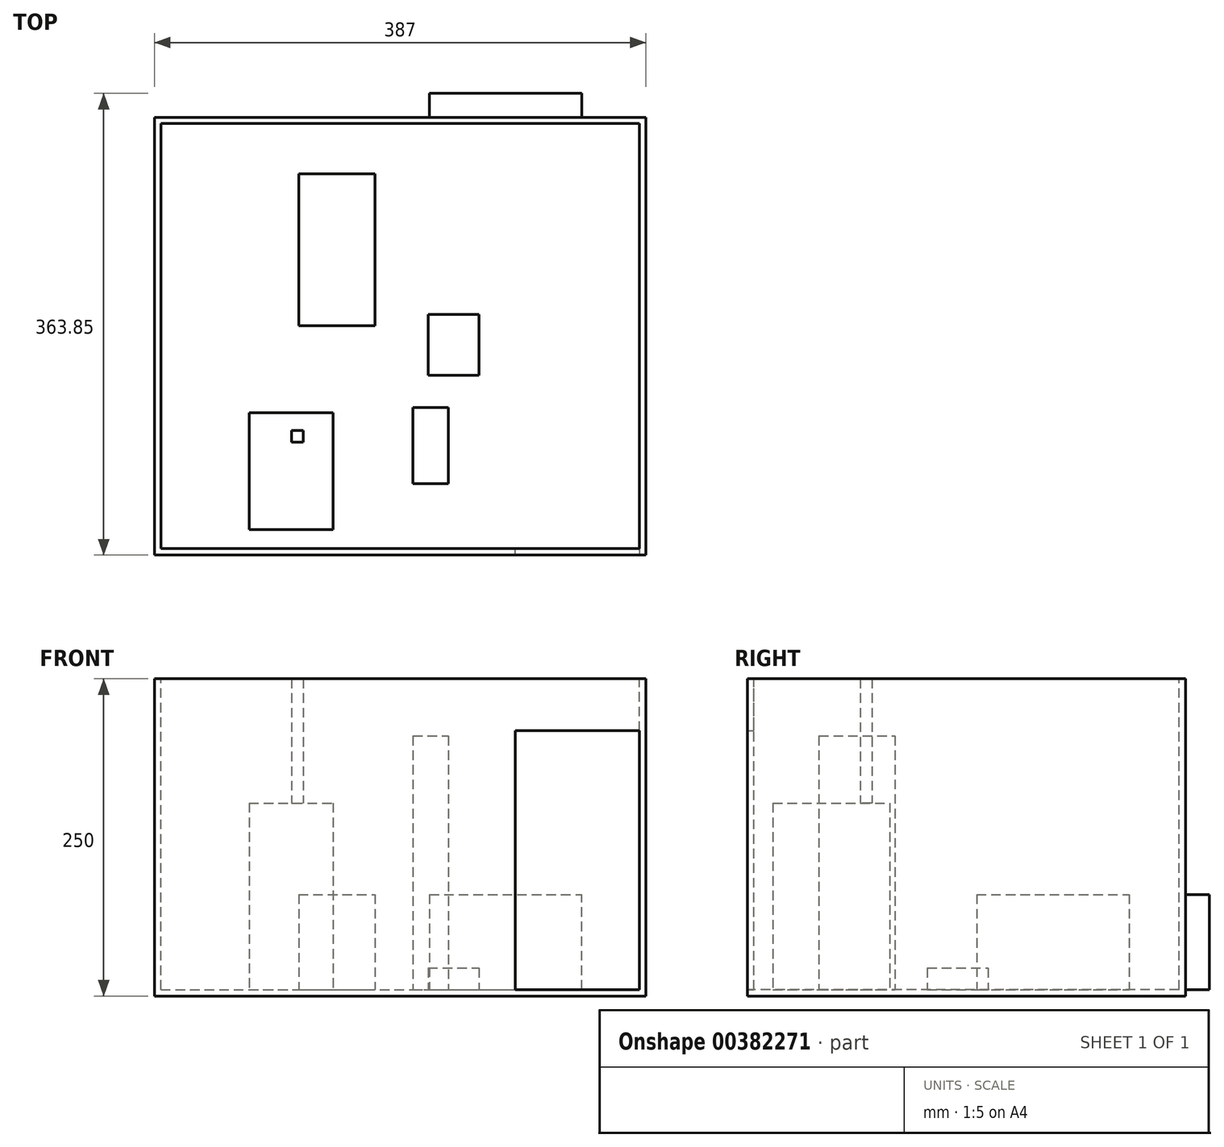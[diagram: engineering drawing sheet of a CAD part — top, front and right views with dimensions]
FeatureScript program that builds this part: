
annotation { "Feature Type Name" : "Feature", "Feature Type Description" : "" }
export const myFeature = defineFeature(function(context is Context, id is Id, definition is map)
    precondition{}
    {
        {
            var Q0;
            Q0=qCreatedBy(makeId("Top.planeOp"),FACE);
            var sketch = newSketch(context, id + "F0", { "sketchPlane" : qUnion([Q0])});
            skLineSegment(sketch, "E0.bottom", {"start": v(-387, 345) * mm, "end": v(0, 345) * mm});
            skLineSegment(sketch, "E0.top", {"start": v(-387, 0) * mm, "end": v(0, 0) * mm});
            skLineSegment(sketch, "E0.left", {"start": v(-387, 345) * mm, "end": v(-387, 0) * mm});
            skLineSegment(sketch, "E0.right", {"start": v(0, 345) * mm, "end": v(0, 0) * mm});
            skSolve(sketch);
        }
        {
            var Q0;
            Q0=qSketchRegion(id+"F0",true);
            extrude(context, id + "F1", {"entities" : qUnion([Q0]), "depth" : 250 * mm});
        }
        {
            var Q0;
            Q0=makeQuery(id+"F1.opExtrude","CAP_FACE",FACE,{"disambiguationData":[OSD([sQuery(id+"F0.wireOp",EDGE,"E0.bottom"),sQuery(id+"F0.wireOp",EDGE,"E0.top"),sQuery(id+"F0.wireOp",EDGE,"E0.left"),sQuery(id+"F0.wireOp",EDGE,"E0.right")])],"isStart":false});
            var sketch = newSketch(context, id + "F2", { "sketchPlane" : qUnion([Q0])});
            skLineSegment(sketch, "E1.bottom", {"start": v(-382, 340) * mm, "end": v(-5, 340) * mm});
            skLineSegment(sketch, "E1.top", {"start": v(-382, 5) * mm, "end": v(-5, 5) * mm});
            skLineSegment(sketch, "E1.left", {"start": v(-382, 340) * mm, "end": v(-382, 5) * mm});
            skLineSegment(sketch, "E1.right", {"start": v(-5, 340) * mm, "end": v(-5, 5) * mm});
            skSolve(sketch);
        }
        {
            var Q0;
            Q0=qSketchRegion(id+"F2",true);
            extrude(context, id + "F3", {"entities" : qUnion([Q0]), "operationType" : NewBodyOperationType.REMOVE, "oppositeDirection" : true, "depth" : 245 * mm});
        }
        {
            var Q0;
            Q0=makeQuery(id+"F3.boolean.opBoolean","COPY",FACE,{"derivedFrom":makeQuery(id+"F3.opExtrude","SWEPT_FACE",FACE,{"disambiguationData":[OSD([sQuery(id+"F2.wireOp",EDGE,"E1.top")])]})});
            var sketch = newSketch(context, id + "F4", { "sketchPlane" : qUnion([Q0])});
            skLineSegment(sketch, "E2.bottom", {"start": v(5, 5) * mm, "end": v(103, 5) * mm});
            skLineSegment(sketch, "E2.top", {"start": v(5, 209) * mm, "end": v(103, 209) * mm});
            skLineSegment(sketch, "E2.left", {"start": v(5, 5) * mm, "end": v(5, 209) * mm});
            skLineSegment(sketch, "E2.right", {"start": v(103, 5) * mm, "end": v(103, 209) * mm});
            skSolve(sketch);
        }
        {
            var Q0;
            Q0=qSketchRegion(id+"F4",true);
            extrude(context, id + "F5", {"entities" : qUnion([Q0]), "operationType" : NewBodyOperationType.REMOVE, "oppositeDirection" : true, "depth" : 25 * mm});
        }
        {
            var Q0;
            Q0=makeQuery(id+"F5.boolean.opBoolean","MERGE",FACE,{"derivedFrom":[makeQuery(id+"F3.boolean.opBoolean","COPY",FACE,{"derivedFrom":makeQuery(id+"F3.opExtrude","CAP_FACE",FACE,{"disambiguationData":[OSD([sQuery(id+"F2.wireOp",EDGE,"E1.bottom"),sQuery(id+"F2.wireOp",EDGE,"E1.top"),sQuery(id+"F2.wireOp",EDGE,"E1.left"),sQuery(id+"F2.wireOp",EDGE,"E1.right")])],"isStart":false})}),makeQuery(id+"F5.opExtrude","SWEPT_FACE",FACE,{"disambiguationData":[OSD([sQuery(id+"F4.wireOp",EDGE,"E2.bottom")])]})]});
            var sketch = newSketch(context, id + "F6", { "sketchPlane" : qUnion([Q0])});
            skLineSegment(sketch, "E3.bottom", {"start": v(-279, 98) * mm, "end": v(-270, 98) * mm});
            skLineSegment(sketch, "E3.top", {"start": v(-279, 89) * mm, "end": v(-270, 89) * mm});
            skLineSegment(sketch, "E3.left", {"start": v(-279, 98) * mm, "end": v(-279, 89) * mm});
            skLineSegment(sketch, "E3.right", {"start": v(-270, 98) * mm, "end": v(-270, 89) * mm});
            skSolve(sketch);
        }
        {
            var Q0;
            Q0=qSketchRegion(id+"F6",true);
            extrude(context, id + "F7", {"entities" : qUnion([Q0]), "operationType" : NewBodyOperationType.ADD, "depth" : 245 * mm});
        }
        {
            var Q0;
            Q0=makeQuery(id+"F5.boolean.opBoolean","MERGE",FACE,{"derivedFrom":[makeQuery(id+"F3.boolean.opBoolean","COPY",FACE,{"derivedFrom":makeQuery(id+"F3.opExtrude","CAP_FACE",FACE,{"disambiguationData":[OSD([sQuery(id+"F2.wireOp",EDGE,"E1.bottom"),sQuery(id+"F2.wireOp",EDGE,"E1.top"),sQuery(id+"F2.wireOp",EDGE,"E1.left"),sQuery(id+"F2.wireOp",EDGE,"E1.right")])],"isStart":false})}),makeQuery(id+"F5.opExtrude","SWEPT_FACE",FACE,{"disambiguationData":[OSD([sQuery(id+"F4.wireOp",EDGE,"E2.bottom")])]})]});
            var sketch = newSketch(context, id + "F8", { "sketchPlane" : qUnion([Q0])});
            skLineSegment(sketch, "E4.bottom", {"start": v(-273.49, 180.55) * mm, "end": v(-213.49, 180.55) * mm});
            skLineSegment(sketch, "E4.top", {"start": v(-273.49, 300.55) * mm, "end": v(-213.49, 300.55) * mm});
            skLineSegment(sketch, "E4.left", {"start": v(-273.49, 180.55) * mm, "end": v(-273.49, 300.55) * mm});
            skLineSegment(sketch, "E4.right", {"start": v(-213.49, 180.55) * mm, "end": v(-213.49, 300.55) * mm});
            skSolve(sketch);
        }
        {
            var Q0;
            Q0=qSketchRegion(id+"F8",true);
            extrude(context, id + "F9", {"entities" : qUnion([Q0]), "operationType" : NewBodyOperationType.ADD, "depth" : 75 * mm});
        }
        {
            var Q0;
            Q0=makeQuery(id+"F5.boolean.opBoolean","MERGE",FACE,{"derivedFrom":[makeQuery(id+"F3.boolean.opBoolean","COPY",FACE,{"derivedFrom":makeQuery(id+"F3.opExtrude","CAP_FACE",FACE,{"disambiguationData":[OSD([sQuery(id+"F2.wireOp",EDGE,"E1.bottom"),sQuery(id+"F2.wireOp",EDGE,"E1.top"),sQuery(id+"F2.wireOp",EDGE,"E1.left"),sQuery(id+"F2.wireOp",EDGE,"E1.right")])],"isStart":false})}),makeQuery(id+"F5.opExtrude","SWEPT_FACE",FACE,{"disambiguationData":[OSD([sQuery(id+"F4.wireOp",EDGE,"E2.bottom")])]})]});
            var sketch = newSketch(context, id + "F10", { "sketchPlane" : qUnion([Q0])});
            skLineSegment(sketch, "E5", {"start": v(-50.35, 171.85) * mm, "end": v(-50.35, 363.85) * mm});
            skLineSegment(sketch, "E6", {"start": v(-50.35, 363.85) * mm, "end": v(-170.35, 363.85) * mm});
            skLineSegment(sketch, "E7", {"start": v(-170.35, 363.85) * mm, "end": v(-170.35, 303.85) * mm});
            skLineSegment(sketch, "E8", {"start": v(-170.35, 303.85) * mm, "end": v(-160.35, 303.85) * mm});
            skLineSegment(sketch, "E9", {"start": v(-130.35, 273.85) * mm, "end": v(-130.35, 199.55) * mm});
            skLineSegment(sketch, "E10", {"start": v(-50.35, 171.85) * mm, "end": v(-95.35, 171.85) * mm});
            skArc(sketch, "E11", {"start": v(-130.35, 199.55) * mm, "mid": v(-117.67, 179.61) * mm, "end": v(-95.35, 171.85) * mm});
            skPoint(sketch, "E12.visualSharp", {"position": v(-130.35, 303.85) * mm});
            skArc(sketch, "E12.filletArc", {"start": v(-130.35, 273.85) * mm, "mid": v(-139.13, 295.06) * mm, "end": v(-160.35, 303.85) * mm});
            skSolve(sketch);
        }
        {
            var Q0;
            Q0=makeQuery(id+"F10.imprint","IMPRINT",FACE,{"disambiguationData":[TD([[makeQuery(id+"F10.imprint","IMPRINT",EDGE,{"derivedFrom":sQuery(id+"F10.wireOp",EDGE,"E5")}),1.0]])]});
            extrude(context, id + "F11", {"entities" : qUnion([Q0]), "operationType" : NewBodyOperationType.ADD, "depth" : 75 * mm});
        }
        {
            var Q0;
            Q0=makeQuery(id+"F5.boolean.opBoolean","MERGE",FACE,{"derivedFrom":[makeQuery(id+"F3.boolean.opBoolean","COPY",FACE,{"derivedFrom":makeQuery(id+"F3.opExtrude","CAP_FACE",FACE,{"disambiguationData":[OSD([sQuery(id+"F2.wireOp",EDGE,"E1.bottom"),sQuery(id+"F2.wireOp",EDGE,"E1.top"),sQuery(id+"F2.wireOp",EDGE,"E1.left"),sQuery(id+"F2.wireOp",EDGE,"E1.right")])],"isStart":false})}),makeQuery(id+"F5.opExtrude","SWEPT_FACE",FACE,{"disambiguationData":[OSD([sQuery(id+"F4.wireOp",EDGE,"E2.bottom")])]})]});
            var sketch = newSketch(context, id + "F12", { "sketchPlane" : qUnion([Q0])});
            skLineSegment(sketch, "E13.bottom", {"start": v(-171.52, 141.65) * mm, "end": v(-131.52, 141.65) * mm});
            skLineSegment(sketch, "E13.top", {"start": v(-171.52, 189.65) * mm, "end": v(-131.52, 189.65) * mm});
            skLineSegment(sketch, "E13.left", {"start": v(-171.52, 141.65) * mm, "end": v(-171.52, 189.65) * mm});
            skLineSegment(sketch, "E13.right", {"start": v(-131.52, 141.65) * mm, "end": v(-131.52, 189.65) * mm});
            skSolve(sketch);
        }
        {
            var Q0;
            Q0=makeQuery(id+"F12.imprint","IMPRINT",FACE,{"disambiguationData":[TD([[makeQuery(id+"F12.imprint","IMPRINT",EDGE,{"derivedFrom":sQuery(id+"F12.wireOp",EDGE,"E13.bottom")}),1.0]])]});
            extrude(context, id + "F13", {"entities" : qUnion([Q0]), "depth" : 17 * mm});
        }
        {
            var Q0;
            Q0=makeQuery(id+"F5.boolean.opBoolean","MERGE",FACE,{"derivedFrom":[makeQuery(id+"F3.boolean.opBoolean","COPY",FACE,{"derivedFrom":makeQuery(id+"F3.opExtrude","CAP_FACE",FACE,{"disambiguationData":[OSD([sQuery(id+"F2.wireOp",EDGE,"E1.bottom"),sQuery(id+"F2.wireOp",EDGE,"E1.top"),sQuery(id+"F2.wireOp",EDGE,"E1.left"),sQuery(id+"F2.wireOp",EDGE,"E1.right")])],"isStart":false})}),makeQuery(id+"F5.opExtrude","SWEPT_FACE",FACE,{"disambiguationData":[OSD([sQuery(id+"F4.wireOp",EDGE,"E2.bottom")])]})]});
            var sketch = newSketch(context, id + "F14", { "sketchPlane" : qUnion([Q0])});
            skLineSegment(sketch, "E14.bottom", {"start": v(-183.5, 56.33) * mm, "end": v(-155.5, 56.33) * mm});
            skLineSegment(sketch, "E14.top", {"start": v(-183.5, 116.33) * mm, "end": v(-155.5, 116.33) * mm});
            skLineSegment(sketch, "E14.left", {"start": v(-183.5, 56.33) * mm, "end": v(-183.5, 116.33) * mm});
            skLineSegment(sketch, "E14.right", {"start": v(-155.5, 56.33) * mm, "end": v(-155.5, 116.33) * mm});
            skSolve(sketch);
        }
        {
            var Q0;
            Q0=qSketchRegion(id+"F14",true);
            extrude(context, id + "F15", {"entities" : qUnion([Q0]), "operationType" : NewBodyOperationType.ADD, "depth" : 200 * mm});
        }
        {
            var Q0;
            Q0=makeQuery(id+"F5.boolean.opBoolean","MERGE",FACE,{"derivedFrom":[makeQuery(id+"F3.boolean.opBoolean","COPY",FACE,{"derivedFrom":makeQuery(id+"F3.opExtrude","CAP_FACE",FACE,{"disambiguationData":[OSD([sQuery(id+"F2.wireOp",EDGE,"E1.bottom"),sQuery(id+"F2.wireOp",EDGE,"E1.top"),sQuery(id+"F2.wireOp",EDGE,"E1.left"),sQuery(id+"F2.wireOp",EDGE,"E1.right")])],"isStart":false})}),makeQuery(id+"F5.opExtrude","SWEPT_FACE",FACE,{"disambiguationData":[OSD([sQuery(id+"F4.wireOp",EDGE,"E2.bottom")])]})]});
            var sketch = newSketch(context, id + "F16", { "sketchPlane" : qUnion([Q0])});
            skLineSegment(sketch, "E15.bottom", {"start": v(-312.46, 20.06) * mm, "end": v(-246.46, 20.06) * mm});
            skLineSegment(sketch, "E15.top", {"start": v(-312.46, 112.06) * mm, "end": v(-246.46, 112.06) * mm});
            skLineSegment(sketch, "E15.left", {"start": v(-312.46, 20.06) * mm, "end": v(-312.46, 112.06) * mm});
            skLineSegment(sketch, "E15.right", {"start": v(-246.46, 20.06) * mm, "end": v(-246.46, 112.06) * mm});
            skSolve(sketch);
        }
        {
            var Q0;
            Q0=makeQuery(id+"F16.imprint","IMPRINT",FACE,{"disambiguationData":[TD([[makeQuery(id+"F16.imprint","IMPRINT",EDGE,{"derivedFrom":sQuery(id+"F16.wireOp",EDGE,"E15.bottom")}),1.0]])]});
            extrude(context, id + "F17", {"entities" : qUnion([Q0]), "operationType" : NewBodyOperationType.ADD, "depth" : 147 * mm});
        }
    });
